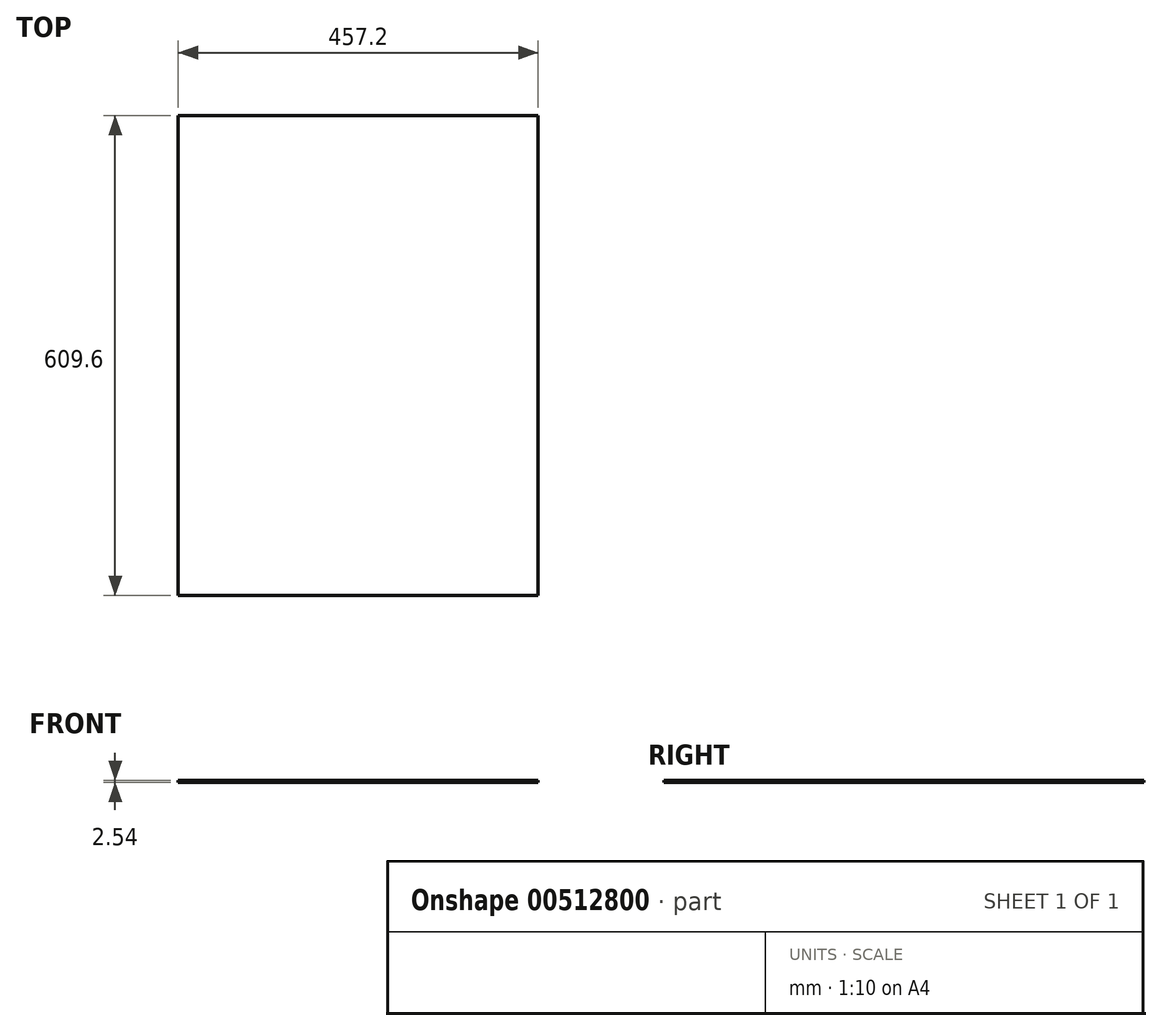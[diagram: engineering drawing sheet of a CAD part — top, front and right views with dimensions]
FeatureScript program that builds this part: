
annotation { "Feature Type Name" : "Feature", "Feature Type Description" : "" }
export const myFeature = defineFeature(function(context is Context, id is Id, definition is map)
    precondition{}
    {
        {
            var Q0;
            Q0=qCreatedBy(makeId("Top.planeOp"),FACE);
            var sketch = newSketch(context, id + "F0", { "sketchPlane" : qUnion([Q0])});
            skLineSegment(sketch, "E0.bottom", {"start": v(228.6, 297.63) * mm, "end": v(-228.6, 297.63) * mm});
            skLineSegment(sketch, "E0.top", {"start": v(228.6, -311.97) * mm, "end": v(-228.6, -311.97) * mm});
            skLineSegment(sketch, "E0.left", {"start": v(228.6, 297.63) * mm, "end": v(228.6, -311.97) * mm});
            skLineSegment(sketch, "E0.right", {"start": v(-228.6, 297.63) * mm, "end": v(-228.6, -311.97) * mm});
            skPoint(sketch, "E0.middle", {"position": v(0, -7.17) * mm});
            skSolve(sketch);
        }
        {
            var Q0;
            Q0=makeQuery(id+"F0.imprint","IMPRINT",FACE,{"disambiguationData":[TD([[makeQuery(id+"F0.imprint","IMPRINT",EDGE,{"derivedFrom":sQuery(id+"F0.wireOp",EDGE,"E0.bottom")}),1.0]])]});
            extrude(context, id + "F1", {"entities" : qUnion([Q0]), "depth" : 2.54 * mm});
        }
    });
